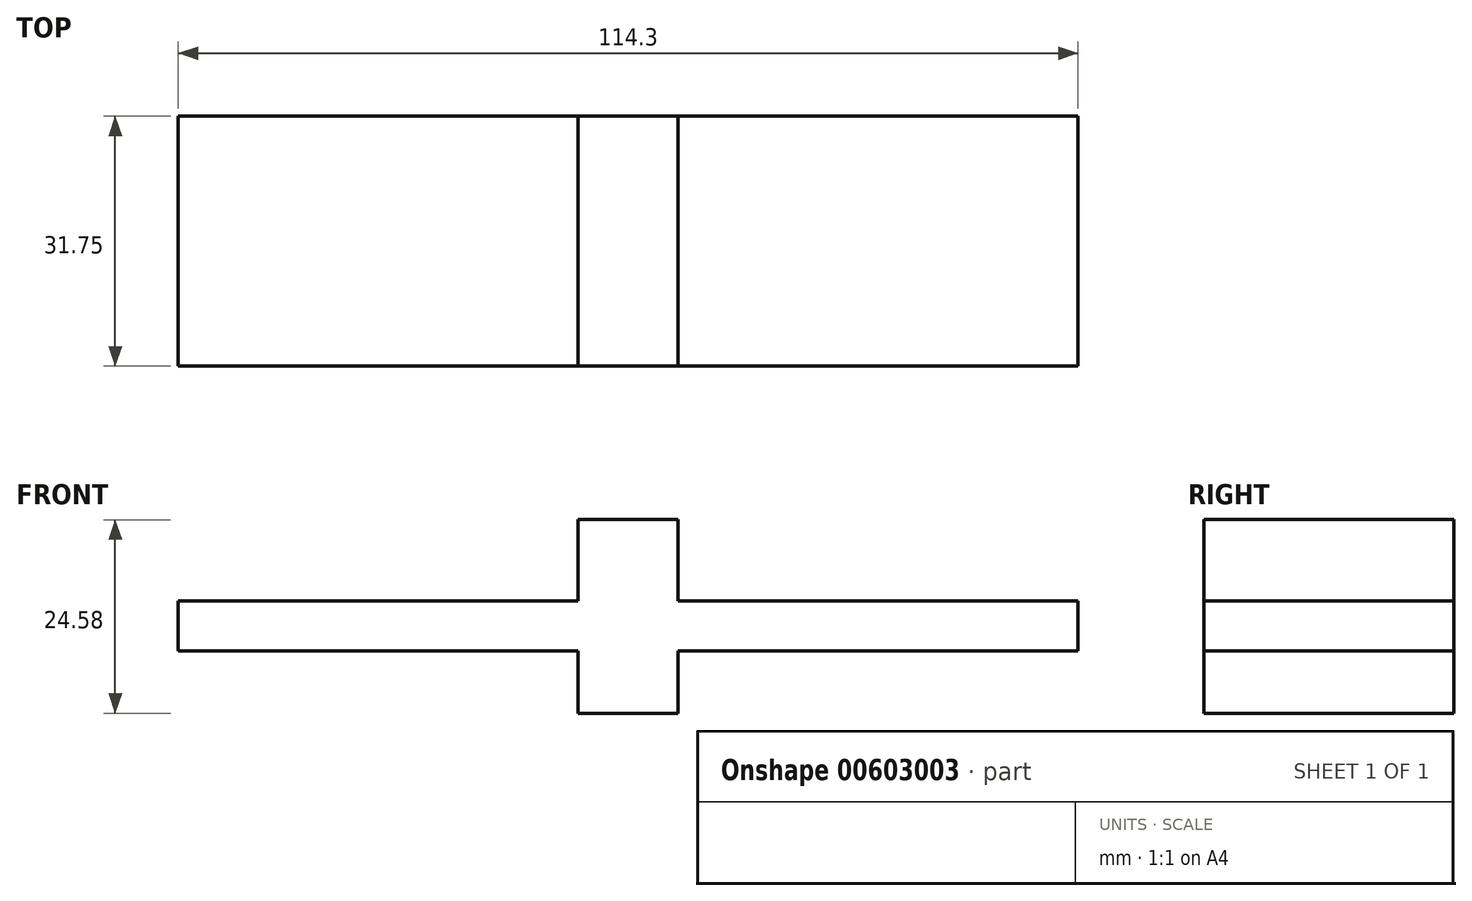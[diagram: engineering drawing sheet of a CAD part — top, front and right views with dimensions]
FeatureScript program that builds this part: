
annotation { "Feature Type Name" : "Feature", "Feature Type Description" : "" }
export const myFeature = defineFeature(function(context is Context, id is Id, definition is map)
    precondition{}
    {
        {
            var Q0;
            Q0=qCreatedBy(makeId("Front.planeOp"),FACE);
            var sketch = newSketch(context, id + "F0", { "sketchPlane" : qUnion([Q0])});
            skLineSegment(sketch, "E0", {"start": v(0, 0) * mm, "end": v(-50.8, 0) * mm});
            skLineSegment(sketch, "E1", {"start": v(-50.8, 0) * mm, "end": v(-50.8, 6.35) * mm});
            skLineSegment(sketch, "E2", {"start": v(-50.8, 6.35) * mm, "end": v(0, 6.35) * mm});
            skLineSegment(sketch, "E3", {"start": v(0, 6.35) * mm, "end": v(0, 16.66) * mm});
            skLineSegment(sketch, "E4", {"start": v(0, 16.66) * mm, "end": v(12.7, 16.66) * mm});
            skLineSegment(sketch, "E5", {"start": v(12.7, 16.66) * mm, "end": v(12.7, 6.35) * mm});
            skLineSegment(sketch, "E6", {"start": v(12.7, 6.35) * mm, "end": v(63.5, 6.35) * mm});
            skLineSegment(sketch, "E7", {"start": v(63.5, 6.35) * mm, "end": v(63.5, 0) * mm});
            skLineSegment(sketch, "E8", {"start": v(63.5, 0) * mm, "end": v(12.7, 0) * mm});
            skLineSegment(sketch, "E9", {"start": v(12.7, 0) * mm, "end": v(12.7, -7.92) * mm});
            skLineSegment(sketch, "E10", {"start": v(12.7, -7.92) * mm, "end": v(0, -7.92) * mm});
            skLineSegment(sketch, "E11", {"start": v(0, -7.92) * mm, "end": v(0, 0) * mm});
            skSolve(sketch);
        }
        {
            var Q0;
            Q0=makeQuery(id+"F0.imprint","IMPRINT",FACE,{"disambiguationData":[TD([[makeQuery(id+"F0.imprint","IMPRINT",EDGE,{"derivedFrom":sQuery(id+"F0.wireOp",EDGE,"E0")}),-1.0]])]});
            extrude(context, id + "F1", {"entities" : qUnion([Q0]), "depth" : 31.75 * mm, "offsetDistance" : 25.4 * mm});
        }
    });
